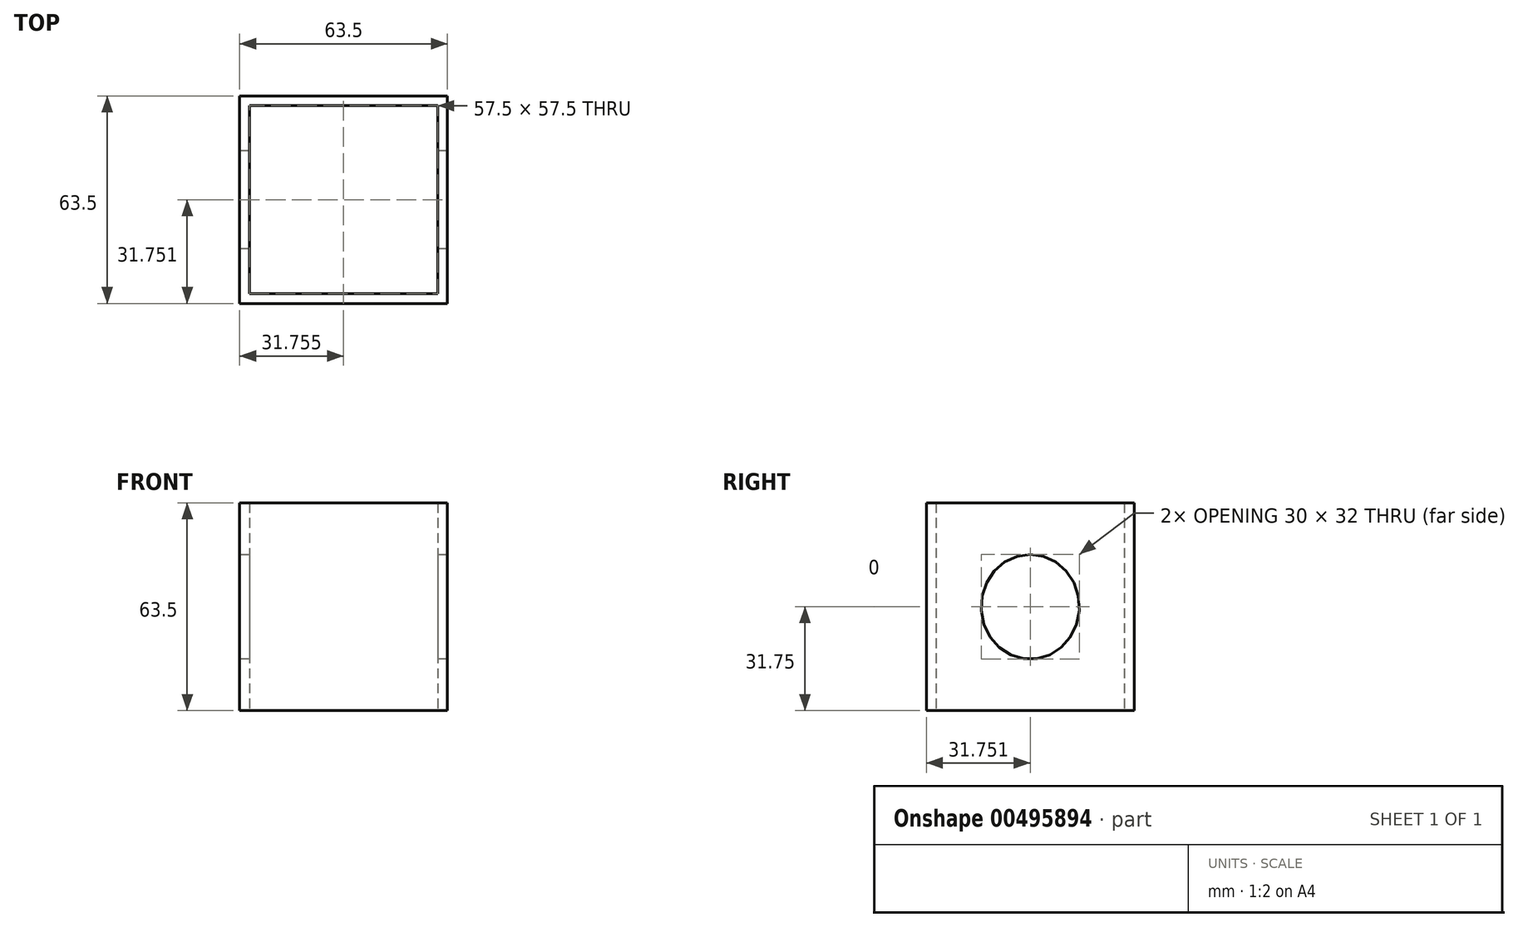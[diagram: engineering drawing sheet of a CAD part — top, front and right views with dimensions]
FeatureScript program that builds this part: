
annotation { "Feature Type Name" : "Feature", "Feature Type Description" : "" }
export const myFeature = defineFeature(function(context is Context, id is Id, definition is map)
    precondition{}
    {
        {
            var Q0;
            Q0=qCreatedBy(makeId("Top.planeOp"),FACE);
            var sketch = newSketch(context, id + "F0", { "sketchPlane" : qUnion([Q0])});
            skLineSegment(sketch, "E0.bottom", {"start": v(-28.45, 29.02) * mm, "end": v(29.05, 29.02) * mm});
            skLineSegment(sketch, "E0.top", {"start": v(-28.45, -28.48) * mm, "end": v(29.05, -28.48) * mm});
            skLineSegment(sketch, "E0.left", {"start": v(-28.45, 29.02) * mm, "end": v(-28.45, -28.48) * mm});
            skLineSegment(sketch, "E0.right", {"start": v(29.05, 29.02) * mm, "end": v(29.05, -28.48) * mm});
            skLineSegment(sketch, "E1.bottom", {"start": v(-31.45, 32.02) * mm, "end": v(32.05, 32.02) * mm});
            skLineSegment(sketch, "E1.top", {"start": v(-31.45, -31.48) * mm, "end": v(32.05, -31.48) * mm});
            skLineSegment(sketch, "E1.left", {"start": v(-31.45, 32.02) * mm, "end": v(-31.45, -31.48) * mm});
            skLineSegment(sketch, "E1.right", {"start": v(32.05, 32.02) * mm, "end": v(32.05, -31.48) * mm});
            skSolve(sketch);
        }
        {
            var Q0;
            Q0 = qSketchRegion(id + "F0", true);
            extrude(context, id + "F1", {"entities" : qUnion([Q0]), "depth" : 63.5 * mm});
        }
        {
            var Q0;
            Q0=makeQuery(id+"F1.opExtrude","SWEPT_FACE",FACE,{"disambiguationData":[OSD([sQuery(id+"F0.wireOp",EDGE,"E1.right")])]});
            var sketch = newSketch(context, id + "F2", { "sketchPlane" : qUnion([Q0])});
            skEllipse(sketch, "E2", {"center": v(0.27, 31.75) * mm, "majorRadius": 16 * mm, "minorRadius": 15 * mm, "majorAxis": v(0, 1)});
            skSolve(sketch);
        }
        {
            var Q0;
            Q0 = qSketchRegion(id + "F2", true);
            extrude(context, id + "F3", {"entities" : qUnion([Q0]), "operationType" : NewBodyOperationType.REMOVE, "oppositeDirection" : true, "depth" : 70 * mm, "offsetDistance" : 25 * mm});
        }
    });
